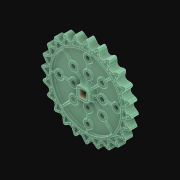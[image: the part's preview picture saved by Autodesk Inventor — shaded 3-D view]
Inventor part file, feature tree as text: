
AUTODESK INVENTOR PART (.ipt)
format: ipt  version: 2021 (Build 250183000, 183)  size: 6,236,160 bytes
history: native  units: in
note: dims shown in document units (in); Inventor stores cm internally (conversion verified against a paired STEP export)
features: sketch x1, other x1, fillet x1, extrude x1
ambient origin geometry x8: Origin, YZ Plane, XZ Plane, XY Plane, X Axis, Y Axis, Z Axis, Center Point
bodies: Solid1 (feature_tree)
feature tree (4):
  sketch  "Sketch1"
  other  "Srf1"
  fillet  "Fillet7"  Radius=0.3937in
  extrude  "ExtrusionSrf1"  [1 undecoded]
note: 1 required parameter value undecoded (feature->parameter linkage not recoverable at this tier; creation-order binding heuristic only, values carry confidence <= 0.55)
